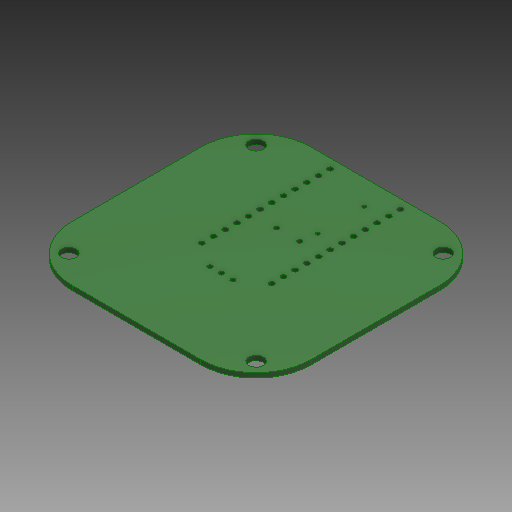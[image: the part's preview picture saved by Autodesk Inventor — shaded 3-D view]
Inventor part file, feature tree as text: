
AUTODESK INVENTOR PART (.ipt)
format: ipt  version: 2018 (Build 220112000, 112)  size: 188,928 bytes
history: native  units: mm
features: extrude x1, sketch x1, projected_geometry x1, imported_body x1
ambient origin geometry x8: Origin, YZ Plane, XZ Plane, XY Plane, X Axis, Y Axis, Z Axis, Center Point
bodies: Volumenkörper1 (feature_tree)
feature tree (4):
  extrude  "Extrusion1"  [1 undecoded]
  sketch  "Skizze1"  dims[d0=0.6mm d1=0.0mm]
  projected_geometry  "Projizierte Kontur1"
  imported_body  "Basis1"
note: 1 required parameter value undecoded (feature->parameter linkage not recoverable at this tier; creation-order binding heuristic only, values carry confidence <= 0.55)
